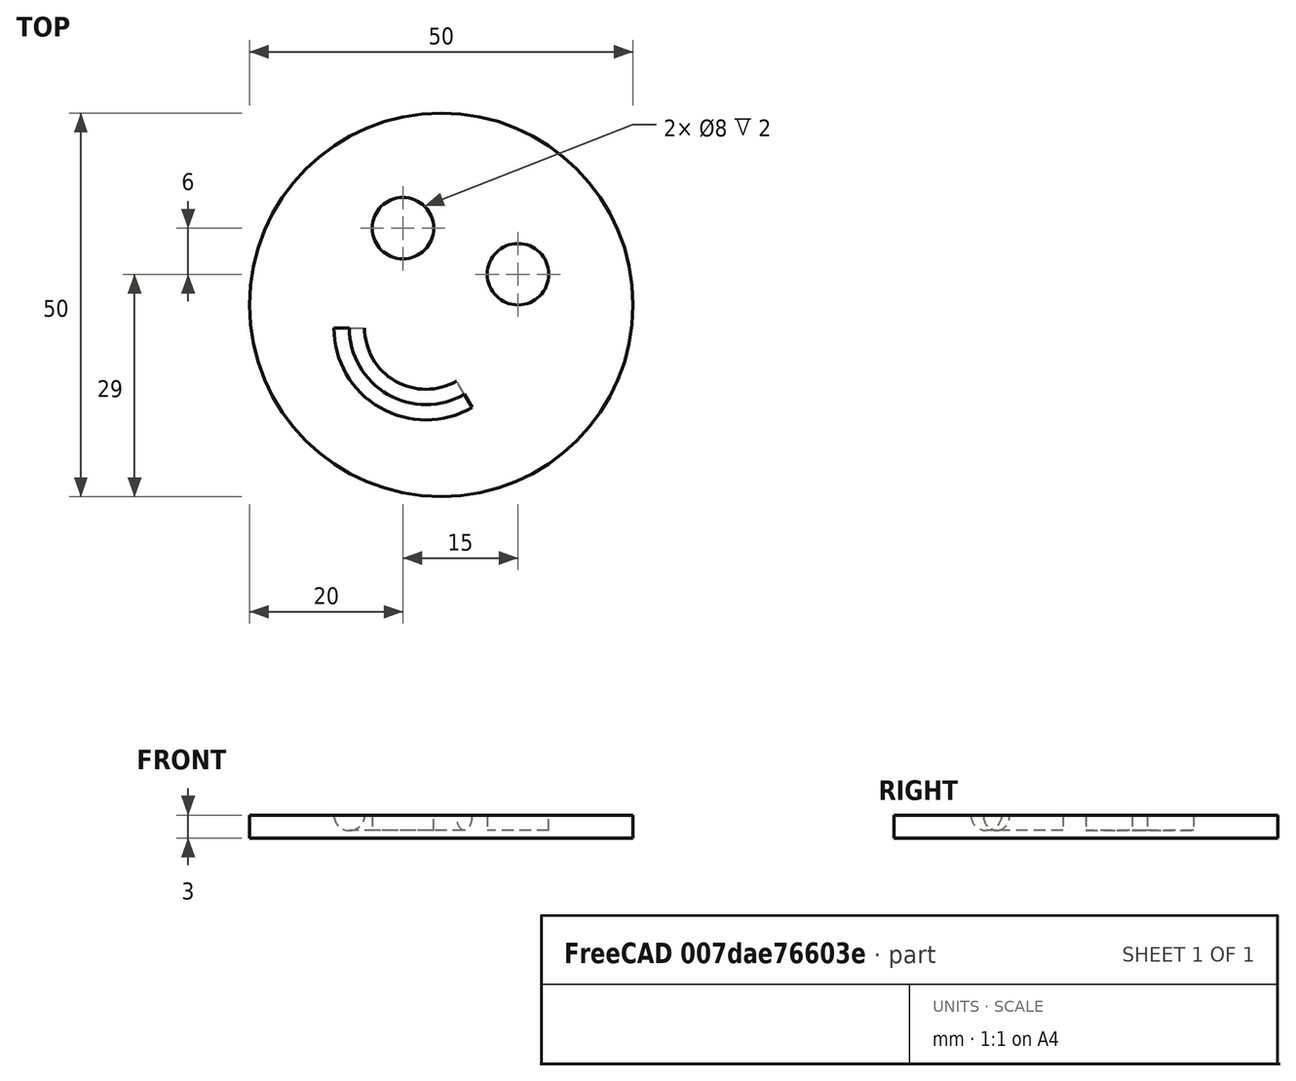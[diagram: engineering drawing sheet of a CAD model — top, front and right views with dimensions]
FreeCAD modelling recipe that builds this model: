
FCSTD DOCUMENT  (FreeCAD 0.21R33694 (Git))
Label: OJT1_T15R01_smiley
License: All rights reserved
LicenseURL: https://en.wikipedia.org/wiki/All_rights_reserved
objects: Part::Cylinder×3, Part::Cut×3, Part::Torus×1
note: 7 computed .brp shape members not serialized (recipe doc carries the construction recipe); baked Part::Feature solids carry a one-line shape summary decoded from their .brp

FEATURE [Part::Cylinder] Cylinder002  label="Ull_1"
  Angle = 360
  AttacherType = Attacher::AttachEngine3D
  FirstAngle = 0
  Height = 2
  Placement = pos=(10,4,1) rot=(0,0,1;0rad)
  Radius = 4
  SecondAngle = 0
FEATURE [Part::Torus] Torus  label="Boca"
  Angle1 = 180
  Angle2 = 180
  Angle3 = 120
  AttacherType = Attacher::AttachEngine3D
  Placement = pos=(-2,-3,3) rot=(0,0,1;3.14159rad)
  Radius1 = 10
  Radius2 = 2
FEATURE [Part::Cylinder] Cylinder  label="Base"
  Angle = 360
  AttacherType = Attacher::AttachEngine3D
  FirstAngle = 0
  Height = 3
  Radius = 25
  SecondAngle = 0
FEATURE [Part::Cylinder] Cylinder003  label="Ull_2"
  Angle = 360
  AttacherType = Attacher::AttachEngine3D
  FirstAngle = 0
  Height = 2
  Placement = pos=(-5,10,1) rot=(0,0,1;0rad)
  Radius = 4
  SecondAngle = 0
FEATURE [Part::Cut] Cut
  Base = -> Cylinder
  Tool = -> Cylinder002
FEATURE [Part::Cut] Cut001
  Base = -> Cut
  Tool = -> Cylinder003
FEATURE [Part::Cut] Cut002
  Base = -> Cut001
  Tool = -> Torus
